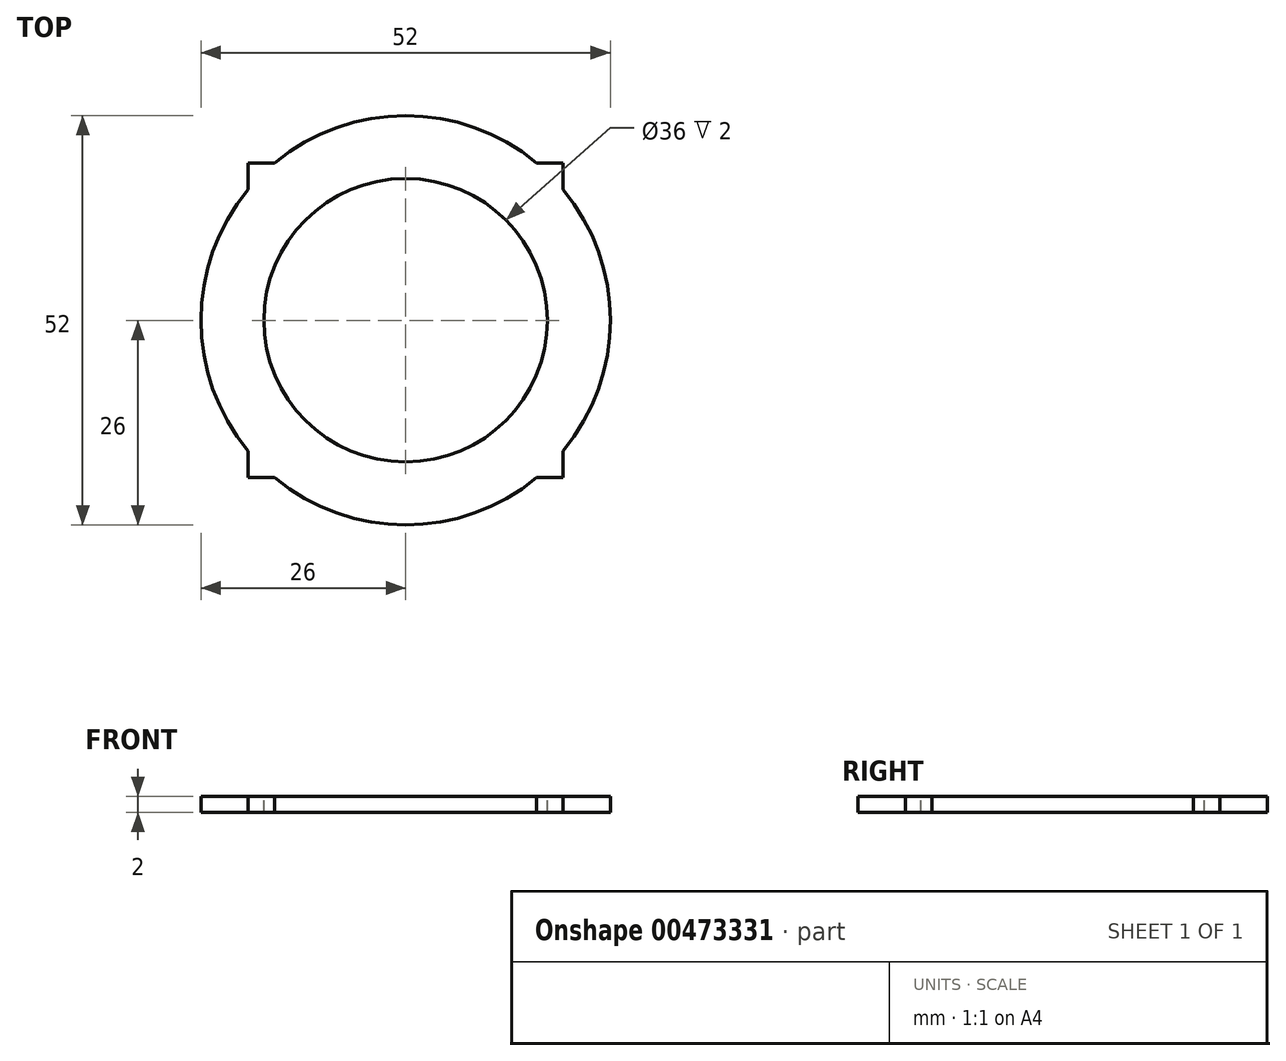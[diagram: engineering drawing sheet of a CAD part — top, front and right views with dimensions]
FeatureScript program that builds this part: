
annotation { "Feature Type Name" : "Feature", "Feature Type Description" : "" }
export const myFeature = defineFeature(function(context is Context, id is Id, definition is map)
    precondition{}
    {
        {
            var Q0;
            Q0=qCreatedBy(makeId("Top.planeOp"),FACE);
            var sketch = newSketch(context, id + "F0", { "sketchPlane" : qUnion([Q0])});
            skLineSegment(sketch, "E0.bottom", {"start": v(20, 20) * mm, "end": v(-20, 20) * mm});
            skLineSegment(sketch, "E0.top", {"start": v(20, -20) * mm, "end": v(-20, -20) * mm});
            skLineSegment(sketch, "E0.left", {"start": v(20, 20) * mm, "end": v(20, -20) * mm});
            skLineSegment(sketch, "E0.right", {"start": v(-20, 20) * mm, "end": v(-20, -20) * mm});
            skPoint(sketch, "E0.middle", {"position": v(0, 0) * mm});
            skSolve(sketch);
        }
        {
            var Q0;
            Q0 = qSketchRegion(id + "F0", true);
            extrude(context, id + "F1", {"entities" : qUnion([Q0]), "depth" : 2 * mm});
        }
        {
            var Q0;
            Q0=qCreatedBy(makeId("Top.planeOp"),FACE);
            var sketch = newSketch(context, id + "F2", { "sketchPlane" : qUnion([Q0])});
            skLineSegment(sketch, "E1.bottom", {"start": v(-16, 20) * mm, "end": v(-14, 20) * mm});
            skLineSegment(sketch, "E1.top", {"start": v(-16, -20) * mm, "end": v(-14, -20) * mm});
            skLineSegment(sketch, "E1.left", {"start": v(-16, 20) * mm, "end": v(-16, -20) * mm});
            skLineSegment(sketch, "E1.right", {"start": v(-14, 20) * mm, "end": v(-14, -20) * mm});
            skLineSegment(sketch, "E2.bottom", {"start": v(-12, 20) * mm, "end": v(-10, 20) * mm});
            skLineSegment(sketch, "E2.top", {"start": v(-12, -20) * mm, "end": v(-10, -20) * mm});
            skLineSegment(sketch, "E2.left", {"start": v(-12, 20) * mm, "end": v(-12, -20) * mm});
            skLineSegment(sketch, "E2.right", {"start": v(-10, 20) * mm, "end": v(-10, -20) * mm});
            skSolve(sketch);
        }
        {
            var Q0;
            Q0 = qSketchRegion(id + "F2", true);
            extrude(context, id + "F3", {"entities" : qUnion([Q0]), "operationType" : NewBodyOperationType.ADD, "depth" : 2 * mm});
        }
        {
            var Q0;
            Q0=qCreatedBy(makeId("Top.planeOp"),FACE);
            var sketch = newSketch(context, id + "F4", { "sketchPlane" : qUnion([Q0])});
            skCircle(sketch, "E3", {"center": v(0, 0) * mm, "radius": 26 * mm});
            skSolve(sketch);
        }
        {
            var Q0;
            Q0 = qSketchRegion(id + "F4", true);
            extrude(context, id + "F5", {"entities" : qUnion([Q0]), "operationType" : NewBodyOperationType.ADD, "depth" : 2 * mm});
        }
        {
            var Q0;
            {var subQ0=sQuery(id+"F0.wireOp",EDGE,"E0.bottom");var subQ2=sQuery(id+"F0.wireOp",EDGE,"E0.top");var subQ4=sQuery(id+"F0.wireOp",EDGE,"E0.right");var subQ5=sQuery(id+"F0.wireOp",EDGE,"E0.left");var subQ6=makeQuery(id+"F1.opExtrude","CAP_FACE",FACE,{"disambiguationData":[OSD([subQ0,subQ2,subQ5,subQ4])],"isStart":false});Q0=makeQuery(id+"F5.boolean.opBoolean","MERGE",FACE,{"derivedFrom":[makeQuery(id+"F3.boolean.opBoolean","SPLIT",FACE,{"disambiguationData":[TD([makeQuery(id+"F1.opExtrude","SWEPT_FACE",FACE,{"disambiguationData":[OSD([subQ5])]})])],"derivedFrom":subQ6}),makeQuery(id+"F3.boolean.opBoolean","SPLIT",FACE,{"disambiguationData":[TD([makeQuery(id+"F1.opExtrude","SWEPT_FACE",FACE,{"disambiguationData":[OSD([subQ4])]})])],"derivedFrom":subQ6}),makeQuery(id+"F3.boolean.opBoolean","SPLIT",FACE,{"disambiguationData":[TD([makeQuery(id+"F3.opExtrude","SWEPT_FACE",FACE,{"disambiguationData":[OSD([sQuery(id+"F2.wireOp",EDGE,"E1.right")])]})])],"derivedFrom":subQ6}),makeQuery(id+"F5.opExtrude","CAP_FACE",FACE,{"disambiguationData":[OSD([sQuery(id+"F4.wireOp",EDGE,"E3")])],"isStart":false})]});}
            var sketch = newSketch(context, id + "F6", { "sketchPlane" : qUnion([Q0])});
            skCircle(sketch, "E4", {"center": v(0, 0) * mm, "radius": 18 * mm});
            skSolve(sketch);
        }
        {
            var Q0;
            Q0 = qSketchRegion(id + "F6", true);
            extrude(context, id + "F7", {"entities" : qUnion([Q0]), "operationType" : NewBodyOperationType.REMOVE, "oppositeDirection" : true, "depth" : 25 * mm});
        }
    });
